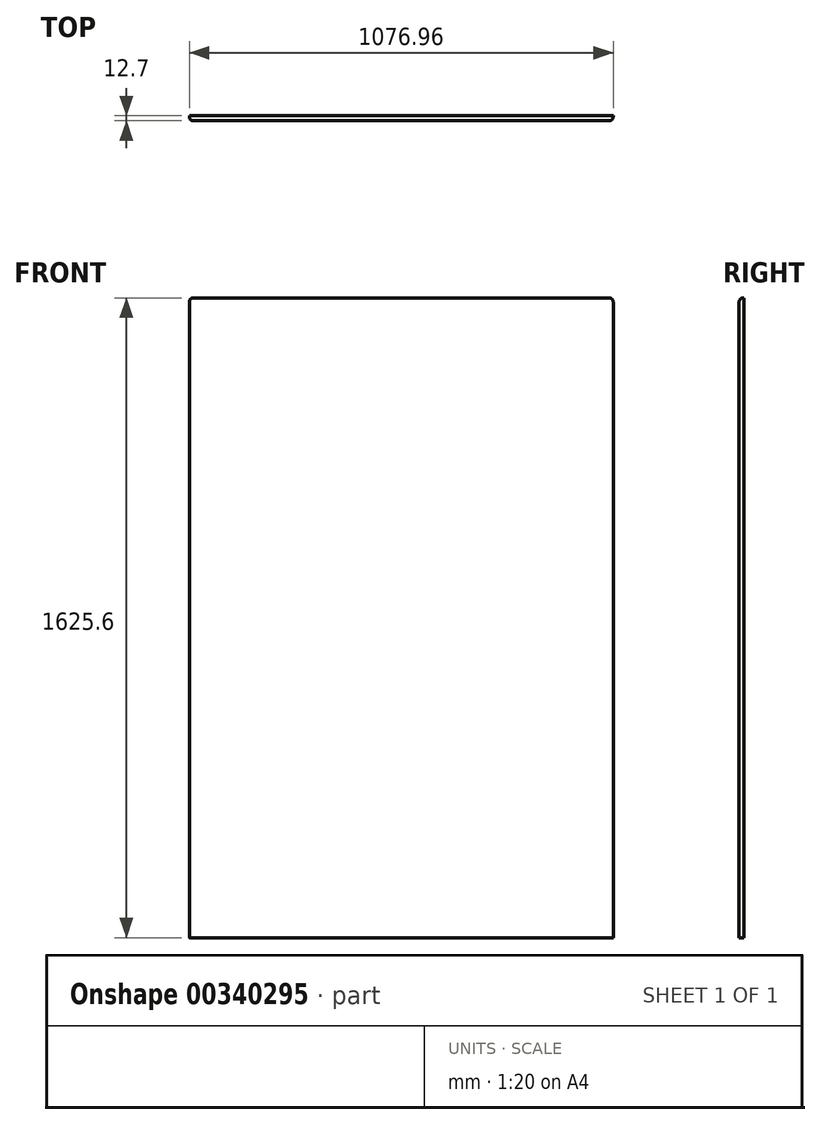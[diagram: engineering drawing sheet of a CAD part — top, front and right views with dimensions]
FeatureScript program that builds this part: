
annotation { "Feature Type Name" : "Feature", "Feature Type Description" : "" }
export const myFeature = defineFeature(function(context is Context, id is Id, definition is map)
    precondition{}
    {
        {
            var Q0;
            Q0=qCreatedBy(makeId("Front.planeOp"),FACE);
            var sketch = newSketch(context, id + "F0", { "sketchPlane" : qUnion([Q0])});
            skLineSegment(sketch, "E0.bottom", {"start": v(538.48, -812.8) * mm, "end": v(-538.48, -812.8) * mm});
            skLineSegment(sketch, "E0.top", {"start": v(538.48, 812.8) * mm, "end": v(-538.48, 812.8) * mm});
            skLineSegment(sketch, "E0.left", {"start": v(538.48, -812.8) * mm, "end": v(538.48, 812.8) * mm});
            skLineSegment(sketch, "E0.right", {"start": v(-538.48, -812.8) * mm, "end": v(-538.48, 812.8) * mm});
            skPoint(sketch, "E0.middle", {"position": v(0, 0) * mm});
            skSolve(sketch);
        }
        {
            var Q0;
            Q0 = qSketchRegion(id + "F0", true);
            extrude(context, id + "F1", {"entities" : qUnion([Q0]), "depth" : 12.7 * mm});
        }
        {
            var Q0;
            Q0=makeQuery(id+"F1.opExtrude","CAP_EDGE",EDGE,{"disambiguationData":[OSD([sQuery(id+"F0.wireOp",EDGE,"E0.top")])],"isStart":false});
            fillet(context, id + "F2", {"entities" : qUnion([Q0]), "radius" : 10.16 * mm, "tangentPropagation" : true, "allowEdgeOverflow" : false});
        }
        {
            var Q0;
            Q0=makeQuery(id+"F1.opExtrude","CAP_EDGE",EDGE,{"disambiguationData":[OSD([sQuery(id+"F0.wireOp",EDGE,"E0.left")])],"isStart":false});
            var Q1;
            Q1=makeQuery(id+"F1.opExtrude","CAP_EDGE",EDGE,{"disambiguationData":[OSD([sQuery(id+"F0.wireOp",EDGE,"E0.right")])],"isStart":false});
            fillet(context, id + "F3", {"entities" : qUnion([Q0, Q1]), "radius" : 10.16 * mm, "tangentPropagation" : true, "allowEdgeOverflow" : false});
        }
    });
